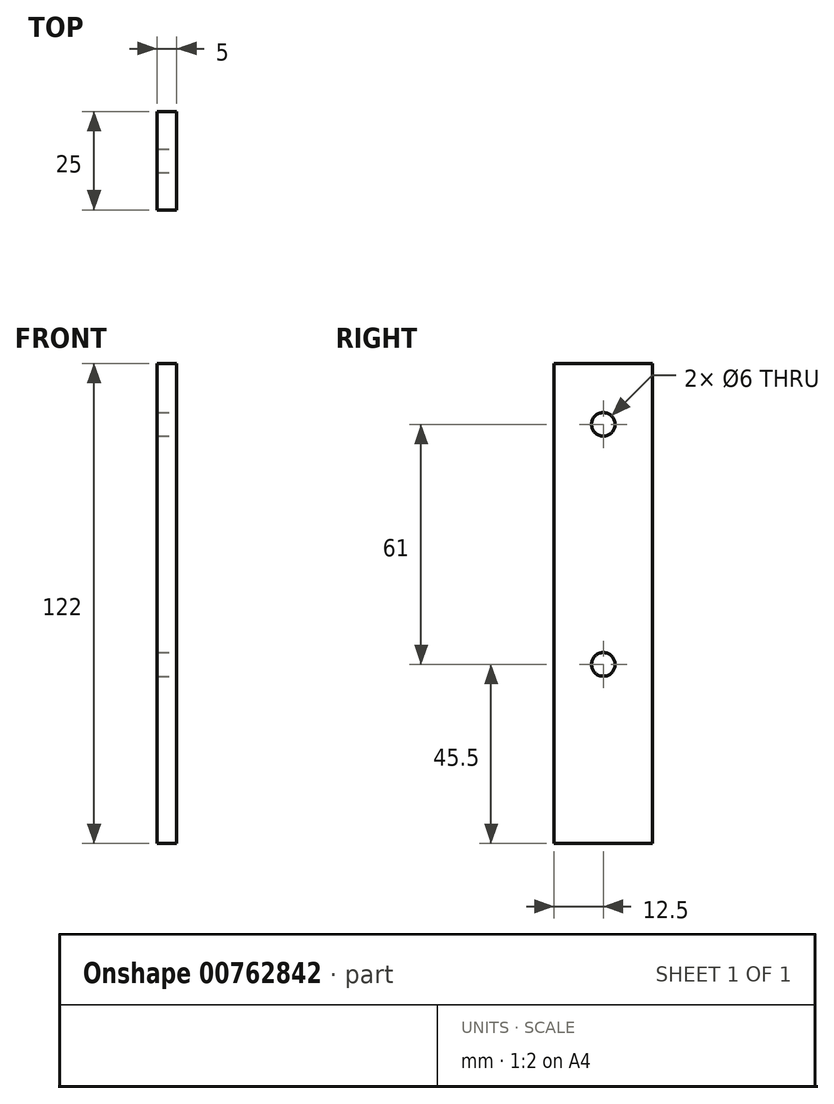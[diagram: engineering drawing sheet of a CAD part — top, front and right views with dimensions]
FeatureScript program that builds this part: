
annotation { "Feature Type Name" : "Feature", "Feature Type Description" : "" }
export const myFeature = defineFeature(function(context is Context, id is Id, definition is map)
    precondition{}
    {
        {
            var Q0;
            Q0=qCreatedBy(makeId("Right.planeOp"),FACE);
            var sketch = newSketch(context, id + "F0", { "sketchPlane" : qUnion([Q0])});
            skLineSegment(sketch, "E0.bottom", {"start": v(0, 0) * mm, "end": v(25, 0) * mm});
            skLineSegment(sketch, "E0.top", {"start": v(0, 122) * mm, "end": v(25, 122) * mm});
            skLineSegment(sketch, "E0.left", {"start": v(0, 0) * mm, "end": v(0, 122) * mm});
            skLineSegment(sketch, "E0.right", {"start": v(25, 0) * mm, "end": v(25, 122) * mm});
            skSolve(sketch);
        }
        {
            var Q0;
            Q0=makeQuery(id+"F0.imprint","IMPRINT",FACE,{"disambiguationData":[TD([[makeQuery(id+"F0.imprint","IMPRINT",EDGE,{"derivedFrom":sQuery(id+"F0.wireOp",EDGE,"E0.bottom")}),1.0]])]});
            extrude(context, id + "F1", {"entities" : qUnion([Q0]), "depth" : 5 * mm, "offsetDistance" : 25 * mm});
        }
        {
            var Q0;
            Q0=makeQuery(id+"F1.opExtrude","CAP_FACE",FACE,{"disambiguationData":[OSD([sQuery(id+"F0.wireOp",EDGE,"E0.bottom"),sQuery(id+"F0.wireOp",EDGE,"E0.top"),sQuery(id+"F0.wireOp",EDGE,"E0.left"),sQuery(id+"F0.wireOp",EDGE,"E0.right")])],"isStart":false});
            var sketch = newSketch(context, id + "F2", { "sketchPlane" : qUnion([Q0])});
            skLineSegment(sketch, "E1", {"start": v(12.5, 122) * mm, "end": v(12.5, 0) * mm, "construction": true});
            skCircle(sketch, "E2", {"center": v(12.5, 106.5) * mm, "radius": 3 * mm});
            skCircle(sketch, "E3", {"center": v(12.5, 45.5) * mm, "radius": 3 * mm});
            skSolve(sketch);
        }
        {
            var Q0;
            Q0 = qSketchRegion(id + "F2", true);
            extrude(context, id + "F3", {"entities" : qUnion([Q0]), "operationType" : NewBodyOperationType.REMOVE, "oppositeDirection" : true, "depth" : 25 * mm, "offsetDistance" : 25 * mm});
        }
    });
